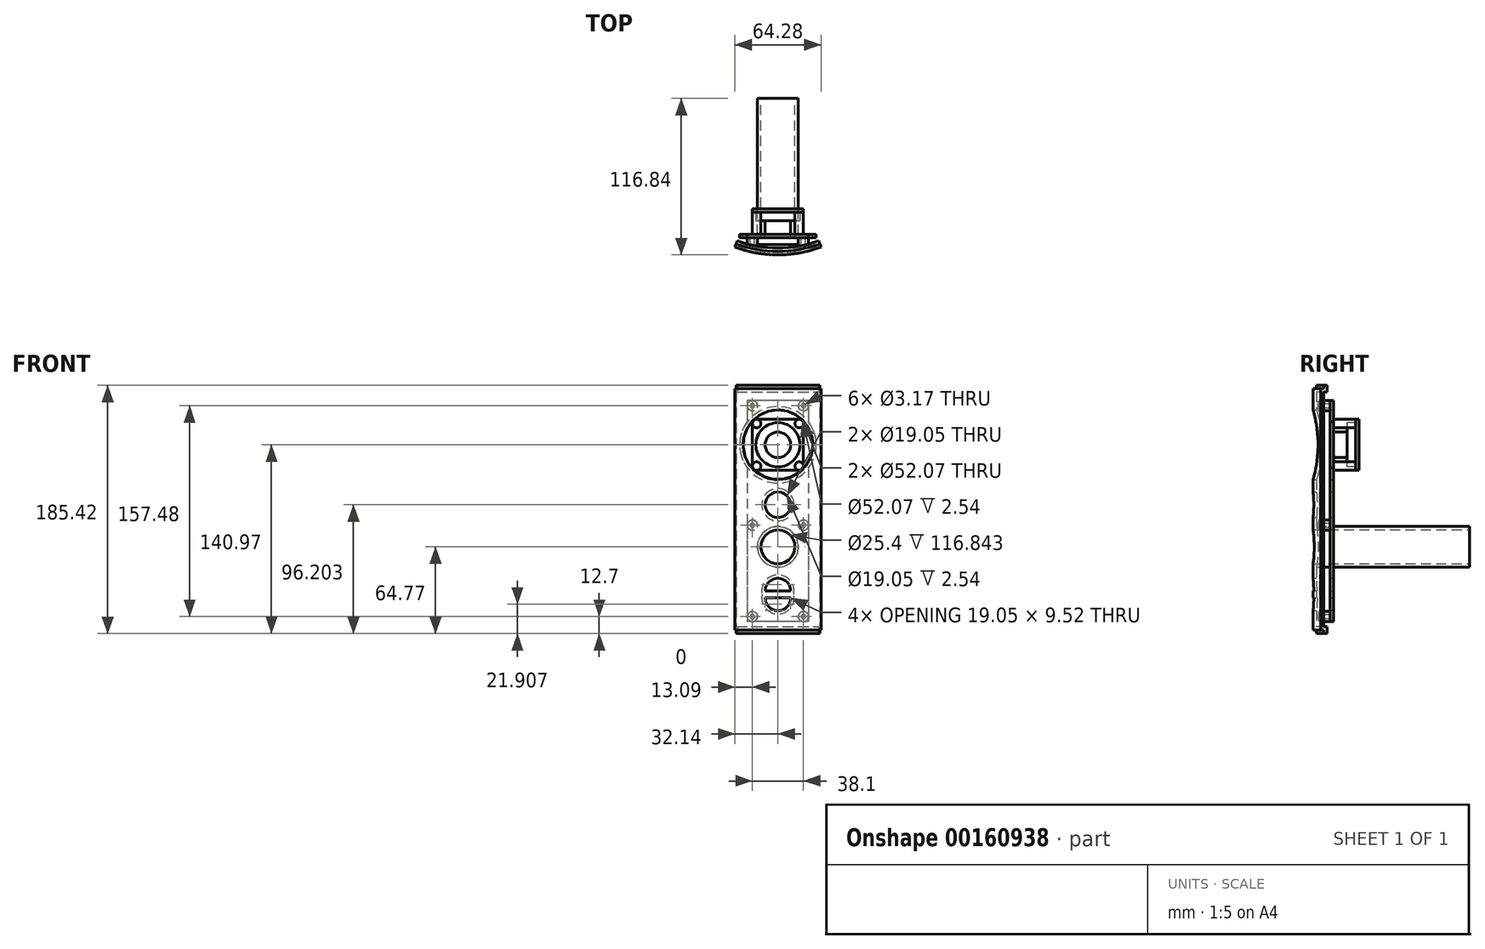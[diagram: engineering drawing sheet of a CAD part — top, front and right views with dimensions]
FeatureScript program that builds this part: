
annotation { "Feature Type Name" : "Feature", "Feature Type Description" : "" }
export const myFeature = defineFeature(function(context is Context, id is Id, definition is map)
    precondition{}
    {
        {
            var Q0;
            Q0=qCreatedBy(makeId("Front.planeOp"),FACE);
            var sketch = newSketch(context, id + "F0", { "sketchPlane" : qUnion([Q0])});
            skLineSegment(sketch, "E0.bottom", {"start": v(22.86, 179.07) * mm, "end": v(-22.86, 179.07) * mm});
            skLineSegment(sketch, "E0.top", {"start": v(22.86, 13.97) * mm, "end": v(-22.86, 13.97) * mm});
            skLineSegment(sketch, "E0.left", {"start": v(22.86, 179.07) * mm, "end": v(22.86, 163.2) * mm});
            skLineSegment(sketch, "E0.right", {"start": v(-22.86, 179.07) * mm, "end": v(-22.86, 163.2) * mm});
            skLineSegment(sketch, "E1", {"start": v(-22.86, 146.05) * mm, "end": v(22.86, 146.05) * mm, "construction": true});
            skCircle(sketch, "E2", {"center": v(0, 146.05) * mm, "radius": 9.53 * mm});
            skCircle(sketch, "E3", {"center": v(0, 146.05) * mm, "radius": 28.58 * mm});
            skCircle(sketch, "E4", {"center": v(0, 69.85) * mm, "radius": 12.7 * mm});
            skCircle(sketch, "E5", {"center": v(0, 69.85) * mm, "radius": 15.24 * mm});
            skPoint(sketch, "E6.endSnap0", {"position": v(0, 13.97) * mm});
            skLineSegment(sketch, "E7", {"start": v(0, 85.1) * mm, "end": v(0, 117.48) * mm, "construction": true});
            skPoint(sketch, "E8", {"position": v(0, 101.28) * mm});
            skCircle(sketch, "E9", {"center": v(0, 101.28) * mm, "radius": 9.53 * mm});
            skLineSegment(sketch, "E10", {"start": v(0, 54.61) * mm, "end": v(0, 13.97) * mm, "construction": true});
            skLineSegment(sketch, "E11", {"start": v(-9.52, 31.75) * mm, "end": v(9.53, 31.75) * mm});
            skPoint(sketch, "E12", {"position": v(0, 34.29) * mm});
            skPoint(sketch, "E13", {"position": v(0, 31.75) * mm});
            skArc(sketch, "E14", {"start": v(-9.52, 31.75) * mm, "mid": v(0, 22.22) * mm, "end": v(9.53, 31.75) * mm});
            skLineSegment(sketch, "E15", {"start": v(-22.86, 34.29) * mm, "end": v(22.86, 34.29) * mm, "construction": true});
            skLineSegment(sketch, "E16.MirrorCS", {"start": v(-9.52, 36.83) * mm, "end": v(9.53, 36.83) * mm});
            skArc(sketch, "E17.MirrorCS", {"start": v(-9.52, 36.83) * mm, "mid": v(0, 46.35) * mm, "end": v(9.53, 36.83) * mm});
            skCircle(sketch, "E18", {"center": v(0, 146.05) * mm, "radius": 26.04 * mm});
            skCircle(sketch, "E19", {"center": v(0, 101.28) * mm, "radius": 12.07 * mm});
            skCircle(sketch, "E20", {"center": v(0, 101.28) * mm, "radius": 6.99 * mm});
            skLineSegment(sketch, "E21.0", {"start": v(-11.8, 34.29) * mm, "end": v(11.8, 34.29) * mm});
            skArc(sketch, "E21.1", {"start": v(-11.8, 34.29) * mm, "mid": v(0, 48.9) * mm, "end": v(11.8, 34.29) * mm});
            skArc(sketch, "E22.1", {"start": v(-11.8, 34.29) * mm, "mid": v(0, 19.68) * mm, "end": v(11.8, 34.29) * mm});
            skLineSegment(sketch, "E23", {"start": v(-6.5, 29.2) * mm, "end": v(6.5, 29.2) * mm});
            skArc(sketch, "E24", {"start": v(-6.5, 29.2) * mm, "mid": v(0, 24.76) * mm, "end": v(6.5, 29.2) * mm});
            skLineSegment(sketch, "E25.MirrorCS", {"start": v(-6.5, 39.37) * mm, "end": v(6.5, 39.37) * mm});
            skArc(sketch, "E26.MirrorCS", {"start": v(-6.5, 39.37) * mm, "mid": v(0, 43.81) * mm, "end": v(6.5, 39.37) * mm});
            skLineSegment(sketch, "E27.MirrorCS", {"start": v(19.05, -58.42) * mm, "end": v(-19.05, -58.42) * mm});
            skLineSegment(sketch, "E28.MirrorCS", {"start": v(19.05, -96.52) * mm, "end": v(19.05, -58.42) * mm});
            skCircle(sketch, "E29", {"center": v(0, 146.05) * mm, "radius": 23.5 * mm});
            skLineSegment(sketch, "E30.trimOffspring", {"start": v(22.86, 128.9) * mm, "end": v(22.86, 13.97) * mm});
            skLineSegment(sketch, "E31.trimOffspring", {"start": v(-22.86, 128.9) * mm, "end": v(-22.86, 13.97) * mm});
            skCircle(sketch, "E32", {"center": v(19.05, 175.26) * mm, "radius": 3.81 * mm});
            skCircle(sketch, "E33", {"center": v(19.05, 175.26) * mm, "radius": 1.59 * mm});
            skCircle(sketch, "E34", {"center": v(-19.05, 175.26) * mm, "radius": 3.81 * mm});
            skCircle(sketch, "E35", {"center": v(-19.05, 175.26) * mm, "radius": 1.59 * mm});
            skCircle(sketch, "E36", {"center": v(-19.05, 17.78) * mm, "radius": 3.81 * mm});
            skCircle(sketch, "E37", {"center": v(-19.05, 17.78) * mm, "radius": 1.59 * mm});
            skCircle(sketch, "E38", {"center": v(19.05, 17.78) * mm, "radius": 3.81 * mm});
            skCircle(sketch, "E39", {"center": v(19.05, 17.78) * mm, "radius": 1.59 * mm});
            skCircle(sketch, "E40", {"center": v(-19.05, 86.04) * mm, "radius": 3.81 * mm});
            skCircle(sketch, "E41", {"center": v(-19.05, 86.04) * mm, "radius": 1.59 * mm});
            skCircle(sketch, "E42", {"center": v(19.05, 86.04) * mm, "radius": 3.81 * mm});
            skCircle(sketch, "E43", {"center": v(19.05, 86.04) * mm, "radius": 1.59 * mm});
            skLineSegment(sketch, "E44", {"start": v(22.86, 86.04) * mm, "end": v(-22.86, 86.04) * mm, "construction": true});
            skCircle(sketch, "E45", {"center": v(0, 146.05) * mm, "radius": 16.51 * mm});
            skSolve(sketch);
        }
        {
            var Q0;
            Q0=qCreatedBy(makeId("Front.planeOp"),FACE);
            var sketch = newSketch(context, id + "F1", { "sketchPlane" : qUnion([Q0])});
            skPoint(sketch, "E46.0", {"position": v(0, 146.05) * mm});
            skLineSegment(sketch, "E47.bottom", {"start": v(-19.05, 165.1) * mm, "end": v(19.05, 165.1) * mm});
            skLineSegment(sketch, "E47.top", {"start": v(-19.05, 127) * mm, "end": v(19.05, 127) * mm});
            skLineSegment(sketch, "E47.left", {"start": v(-19.05, 165.1) * mm, "end": v(-19.05, 127) * mm});
            skLineSegment(sketch, "E47.right", {"start": v(19.05, 165.1) * mm, "end": v(19.05, 127) * mm});
            skCircle(sketch, "E48", {"center": v(-15.88, 130.17) * mm, "radius": 3.18 * mm});
            skCircle(sketch, "E49", {"center": v(-15.88, 161.92) * mm, "radius": 3.18 * mm});
            skCircle(sketch, "E50", {"center": v(15.88, 161.92) * mm, "radius": 3.18 * mm});
            skCircle(sketch, "E51", {"center": v(15.87, 130.17) * mm, "radius": 3.18 * mm});
            skSolve(sketch);
        }
        {
            var Q0;
            {var subQ0=sQuery(id+"F0.wireOp",EDGE,"E0.left");var subQ1=sQuery(id+"F0.wireOp",EDGE,"E0.bottom");var subQ2=makeQuery(id+"F0.imprint","INTERSECT",VERTEX,{"derivedFrom":[subQ1,subQ0]});Q0=makeQuery(id+"F0.imprint","IMPRINT",FACE,{"disambiguationData":[TD([[makeQuery(id+"F0.imprint","IMPRINT",EDGE,{"disambiguationData":[TD([[subQ2,-1.0]])],"derivedFrom":subQ1}),1.0]])]});}
            var Q1;
            {var subQ0=sQuery(id+"F0.wireOp",EDGE,"E0.right");var subQ1=sQuery(id+"F0.wireOp",EDGE,"E0.bottom");var subQ2=makeQuery(id+"F0.imprint","INTERSECT",VERTEX,{"derivedFrom":[subQ1,subQ0]});Q1=makeQuery(id+"F0.imprint","IMPRINT",FACE,{"disambiguationData":[TD([[makeQuery(id+"F0.imprint","IMPRINT",EDGE,{"disambiguationData":[TD([[subQ2,1.0]])],"derivedFrom":subQ1}),1.0]])]});}
            var Q2;
            {var subQ0=sQuery(id+"F0.wireOp",EDGE,"E30.trimOffspring");var subQ1=sQuery(id+"F0.wireOp",EDGE,"E0.top");var subQ2=makeQuery(id+"F0.imprint","INTERSECT",VERTEX,{"derivedFrom":[subQ1,subQ0]});Q2=makeQuery(id+"F0.imprint","IMPRINT",FACE,{"disambiguationData":[TD([[makeQuery(id+"F0.imprint","IMPRINT",EDGE,{"disambiguationData":[TD([[subQ2,-1.0]])],"derivedFrom":subQ1}),-1.0]])]});}
            var Q3;
            {var subQ0=sQuery(id+"F0.wireOp",EDGE,"E31.trimOffspring");var subQ1=sQuery(id+"F0.wireOp",EDGE,"E0.top");var subQ2=makeQuery(id+"F0.imprint","INTERSECT",VERTEX,{"derivedFrom":[subQ1,subQ0]});Q3=makeQuery(id+"F0.imprint","IMPRINT",FACE,{"disambiguationData":[TD([[makeQuery(id+"F0.imprint","IMPRINT",EDGE,{"disambiguationData":[TD([[subQ2,1.0]])],"derivedFrom":subQ1}),-1.0]])]});}
            var Q4;
            Q4=makeQuery(id+"F0.imprint","IMPRINT",FACE,{"disambiguationData":[TD([[makeQuery(id+"F0.imprint","IMPRINT",EDGE,{"derivedFrom":sQuery(id+"F0.wireOp",EDGE,"E11")}),-1.0]])]});
            var Q5;
            Q5=makeQuery(id+"F0.imprint","IMPRINT",FACE,{"disambiguationData":[TD([[makeQuery(id+"F0.imprint","IMPRINT",EDGE,{"derivedFrom":sQuery(id+"F0.wireOp",EDGE,"E16.MirrorCS")}),1.0]])]});
            var Q6;
            Q6=makeQuery(id+"F0.imprint","IMPRINT",FACE,{"disambiguationData":[TD([[makeQuery(id+"F0.imprint","IMPRINT",EDGE,{"derivedFrom":sQuery(id+"F0.wireOp",EDGE,"E9")}),1.0]])]});
            var Q7;
            Q7=makeQuery(id+"F0.imprint","IMPRINT",FACE,{"disambiguationData":[TD([[makeQuery(id+"F0.imprint","IMPRINT",EDGE,{"derivedFrom":sQuery(id+"F0.wireOp",EDGE,"E9")}),-1.0]])]});
            var Q8;
            Q8=makeQuery(id+"F0.imprint","IMPRINT",FACE,{"disambiguationData":[TD([[makeQuery(id+"F0.imprint","IMPRINT",EDGE,{"derivedFrom":sQuery(id+"F0.wireOp",EDGE,"E16.MirrorCS")}),-1.0]])]});
            var Q9;
            Q9=makeQuery(id+"F0.imprint","IMPRINT",FACE,{"disambiguationData":[TD([[makeQuery(id+"F0.imprint","IMPRINT",EDGE,{"derivedFrom":sQuery(id+"F0.wireOp",EDGE,"E25.MirrorCS")}),1.0]])]});
            var Q10;
            Q10=makeQuery(id+"F0.imprint","IMPRINT",FACE,{"disambiguationData":[TD([[makeQuery(id+"F0.imprint","IMPRINT",EDGE,{"derivedFrom":sQuery(id+"F0.wireOp",EDGE,"E2")}),1.0]])]});
            var Q11;
            Q11=makeQuery(id+"F0.imprint","IMPRINT",FACE,{"disambiguationData":[TD([[makeQuery(id+"F0.imprint","IMPRINT",EDGE,{"derivedFrom":sQuery(id+"F0.wireOp",EDGE,"E20")}),1.0]])]});
            var Q12;
            Q12=makeQuery(id+"F0.imprint","IMPRINT",FACE,{"disambiguationData":[TD([[makeQuery(id+"F0.imprint","IMPRINT",EDGE,{"derivedFrom":sQuery(id+"F0.wireOp",EDGE,"E11")}),1.0]])]});
            var Q13;
            Q13=makeQuery(id+"F0.imprint","IMPRINT",FACE,{"disambiguationData":[TD([[makeQuery(id+"F0.imprint","IMPRINT",EDGE,{"derivedFrom":sQuery(id+"F0.wireOp",EDGE,"E23")}),-1.0]])]});
            var Q14;
            Q14=makeQuery(id+"F0.imprint","IMPRINT",FACE,{"disambiguationData":[TD([[makeQuery(id+"F0.imprint","IMPRINT",EDGE,{"derivedFrom":sQuery(id+"F0.wireOp",EDGE,"E2")}),-1.0]])]});
            var Q15;
            Q15=makeQuery(id+"F0.imprint","IMPRINT",FACE,{"disambiguationData":[TD([[makeQuery(id+"F0.imprint","IMPRINT",EDGE,{"derivedFrom":sQuery(id+"F0.wireOp",EDGE,"E18")}),1.0]])]});
            var Q16;
            Q16=makeQuery(id+"F0.imprint","IMPRINT",FACE,{"disambiguationData":[TD([[makeQuery(id+"F0.imprint","IMPRINT",EDGE,{"derivedFrom":sQuery(id+"F0.wireOp",EDGE,"E18")}),-1.0]])]});
            var Q17;
            Q17=makeQuery(id+"F0.imprint","IMPRINT",FACE,{"disambiguationData":[TD([[makeQuery(id+"F0.imprint","IMPRINT",EDGE,{"derivedFrom":sQuery(id+"F0.wireOp",EDGE,"E40")}),1.0]])]});
            var Q18;
            Q18=makeQuery(id+"F0.imprint","IMPRINT",FACE,{"disambiguationData":[TD([[makeQuery(id+"F0.imprint","IMPRINT",EDGE,{"derivedFrom":sQuery(id+"F0.wireOp",EDGE,"E35")}),-1.0]])]});
            var Q19;
            Q19=makeQuery(id+"F0.imprint","IMPRINT",FACE,{"disambiguationData":[TD([[makeQuery(id+"F0.imprint","IMPRINT",EDGE,{"derivedFrom":sQuery(id+"F0.wireOp",EDGE,"E5")}),-1.0]])]});
            var Q20;
            {var subQ7=sQuery(id+"F0.wireOp",EDGE,"E32");var subQ8=sQuery(id+"F0.wireOp",EDGE,"E0.bottom");var subQ9=makeQuery(id+"F0.imprint","INTERSECT",VERTEX,{"derivedFrom":[subQ8,subQ7]});Q20=makeQuery(id+"F0.imprint","IMPRINT",FACE,{"disambiguationData":[TD([[makeQuery(id+"F0.imprint","IMPRINT",EDGE,{"disambiguationData":[TD([[subQ9,-1.0]])],"derivedFrom":subQ8}),1.0]])]});}
            var Q21;
            Q21=makeQuery(id+"F0.imprint","IMPRINT",FACE,{"disambiguationData":[TD([[makeQuery(id+"F0.imprint","IMPRINT",EDGE,{"derivedFrom":sQuery(id+"F0.wireOp",EDGE,"E39")}),-1.0]])]});
            var Q22;
            Q22=makeQuery(id+"F0.imprint","IMPRINT",FACE,{"disambiguationData":[TD([[makeQuery(id+"F0.imprint","IMPRINT",EDGE,{"derivedFrom":sQuery(id+"F0.wireOp",EDGE,"E33")}),-1.0]])]});
            var Q23;
            Q23=makeQuery(id+"F0.imprint","IMPRINT",FACE,{"disambiguationData":[TD([[makeQuery(id+"F0.imprint","IMPRINT",EDGE,{"derivedFrom":sQuery(id+"F0.wireOp",EDGE,"E37")}),-1.0]])]});
            var Q24;
            Q24=makeQuery(id+"F0.imprint","IMPRINT",FACE,{"disambiguationData":[TD([[makeQuery(id+"F0.imprint","IMPRINT",EDGE,{"derivedFrom":sQuery(id+"F0.wireOp",EDGE,"E42")}),1.0]])]});
            var Q25;
            Q25=makeQuery(id+"F0.imprint","IMPRINT",FACE,{"disambiguationData":[TD([[makeQuery(id+"F0.imprint","IMPRINT",EDGE,{"derivedFrom":sQuery(id+"F0.wireOp",EDGE,"E29")}),1.0]])]});
            extrude(context, id + "F2", {"entities" : qUnion([Q0, Q1, Q2, Q3, Q4, Q5, Q6, Q7, Q8, Q9, Q10, Q11, Q12, Q13, Q14, Q15, Q16, Q17, Q18, Q19, Q20, Q21, Q22, Q23, Q24, Q25]), "depth" : 2.54 * mm});
        }
        {
            var Q0;
            {var subQ0=sQuery(id+"F0.wireOp",EDGE,"q9dnOXJF-SNOI-slnn-AHY7-xpP3kkiLgcJX");var subQ1=makeQuery(id+"F0.imprint","INTERSECT",VERTEX,{"derivedFrom":[sQuery(id+"F0.wireOp",EDGE,"DjAzfUVB-9j4b-ZdHd-rkEd-jADuD7Jo3FUt.bottom"),subQ0]});Q0=makeQuery(id+"F0.imprint","IMPRINT",FACE,{"disambiguationData":[TD([[makeQuery(id+"F0.imprint","IMPRINT",EDGE,{"disambiguationData":[TD([[subQ1,1.0]])],"derivedFrom":subQ0}),1.0]])]});}
            var Q1;
            {var subQ0=sQuery(id+"F0.wireOp",EDGE,"a1069b40-808e-4e41-bdb6-6fb071ad80940.MirrorC");var subQ1=makeQuery(id+"F0.imprint","INTERSECT",VERTEX,{"derivedFrom":[sQuery(id+"F0.wireOp",EDGE,"DjAzfUVB-9j4b-ZdHd-rkEd-jADuD7Jo3FUt.top"),subQ0]});Q1=makeQuery(id+"F0.imprint","IMPRINT",FACE,{"disambiguationData":[TD([[makeQuery(id+"F0.imprint","IMPRINT",EDGE,{"disambiguationData":[TD([[subQ1,1.0]])],"derivedFrom":subQ0}),-1.0]])]});}
            var Q2;
            {var subQ0=sQuery(id+"F0.wireOp",EDGE,"9b3ac167-9260-4d4f-b816-18fe052ad9fa0.MirrorC");var subQ1=makeQuery(id+"F0.imprint","INTERSECT",VERTEX,{"derivedFrom":[sQuery(id+"F0.wireOp",EDGE,"DjAzfUVB-9j4b-ZdHd-rkEd-jADuD7Jo3FUt.top"),subQ0]});Q2=makeQuery(id+"F0.imprint","IMPRINT",FACE,{"disambiguationData":[TD([[makeQuery(id+"F0.imprint","IMPRINT",EDGE,{"disambiguationData":[TD([[subQ1,1.0]])],"derivedFrom":subQ0}),1.0]])]});}
            var Q3;
            {var subQ0=sQuery(id+"F1.wireOp",EDGE,"E48");var subQ1=makeQuery(id+"F1.imprint","INTERSECT",VERTEX,{"derivedFrom":[sQuery(id+"F1.wireOp",EDGE,"E47.top"),subQ0]});Q3=makeQuery(id+"F1.imprint","IMPRINT",FACE,{"disambiguationData":[TD([[makeQuery(id+"F1.imprint","IMPRINT",EDGE,{"disambiguationData":[TD([[subQ1,1.0]])],"derivedFrom":subQ0}),1.0]])]});}
            var Q4;
            {var subQ0=sQuery(id+"F1.wireOp",EDGE,"E51");var subQ1=makeQuery(id+"F1.imprint","INTERSECT",VERTEX,{"derivedFrom":[sQuery(id+"F1.wireOp",EDGE,"E47.top"),subQ0]});Q4=makeQuery(id+"F1.imprint","IMPRINT",FACE,{"disambiguationData":[TD([[makeQuery(id+"F1.imprint","IMPRINT",EDGE,{"disambiguationData":[TD([[subQ1,1.0]])],"derivedFrom":subQ0}),1.0]])]});}
            var Q5;
            {var subQ0=sQuery(id+"F1.wireOp",EDGE,"E50");var subQ1=makeQuery(id+"F1.imprint","INTERSECT",VERTEX,{"derivedFrom":[sQuery(id+"F1.wireOp",EDGE,"E47.bottom"),subQ0]});Q5=makeQuery(id+"F1.imprint","IMPRINT",FACE,{"disambiguationData":[TD([[makeQuery(id+"F1.imprint","IMPRINT",EDGE,{"disambiguationData":[TD([[subQ1,1.0]])],"derivedFrom":subQ0}),1.0]])]});}
            var Q6;
            {var subQ0=sQuery(id+"F1.wireOp",EDGE,"E49");var subQ1=makeQuery(id+"F1.imprint","INTERSECT",VERTEX,{"derivedFrom":[sQuery(id+"F1.wireOp",EDGE,"E47.bottom"),subQ0]});Q6=makeQuery(id+"F1.imprint","IMPRINT",FACE,{"disambiguationData":[TD([[makeQuery(id+"F1.imprint","IMPRINT",EDGE,{"disambiguationData":[TD([[subQ1,-1.0]])],"derivedFrom":subQ0}),1.0]])]});}
            extrude(context, id + "F3", {"entities" : qUnion([Q0, Q1, Q2, Q3, Q4, Q5, Q6]), "operationType" : NewBodyOperationType.ADD, "oppositeDirection" : true, "depth" : 19.05 * mm});
        }
        {
            var Q0;
            Q0=makeQuery(id+"F0.imprint","IMPRINT",FACE,{"disambiguationData":[TD([[makeQuery(id+"F0.imprint","IMPRINT",EDGE,{"derivedFrom":sQuery(id+"F0.wireOp",EDGE,"E2")}),1.0]])]});
            extrude(context, id + "F4", {"entities" : qUnion([Q0]), "operationType" : NewBodyOperationType.ADD, "depth" : 16.5 * mm});
        }
        {
            var Q0;
            Q0=makeQuery(id+"F0.imprint","IMPRINT",FACE,{"disambiguationData":[TD([[makeQuery(id+"F0.imprint","IMPRINT",EDGE,{"derivedFrom":sQuery(id+"F0.wireOp",EDGE,"E2")}),1.0]])]});
            extrude(context, id + "F5", {"entities" : qUnion([Q0]), "operationType" : NewBodyOperationType.ADD, "oppositeDirection" : true, "depth" : 17.78 * mm});
        }
        {
            var Q0;
            Q0=makeQuery(id+"F0.imprint","IMPRINT",FACE,{"disambiguationData":[TD([[makeQuery(id+"F0.imprint","IMPRINT",EDGE,{"derivedFrom":sQuery(id+"F0.wireOp",EDGE,"E2")}),-1.0]])]});
            extrude(context, id + "F6", {"entities" : qUnion([Q0]), "operationType" : NewBodyOperationType.ADD, "oppositeDirection" : true, "depth" : 17.78 * mm, "hasSecondDirection" : true, "secondDirectionOppositeDirection" : true, "secondDirectionDepth" : 10.16 * mm});
        }
        {
            var Q0;
            {var subQ0=sQuery(id+"F1.wireOp",EDGE,"E50");var subQ1=makeQuery(id+"F1.imprint","INTERSECT",VERTEX,{"derivedFrom":[sQuery(id+"F1.wireOp",EDGE,"E47.bottom"),subQ0]});Q0=makeQuery(id+"F1.imprint","IMPRINT",FACE,{"disambiguationData":[TD([[makeQuery(id+"F1.imprint","IMPRINT",EDGE,{"disambiguationData":[TD([[subQ1,1.0]])],"derivedFrom":subQ0}),1.0]])]});}
            var Q1;
            {var subQ0=sQuery(id+"F1.wireOp",EDGE,"E49");var subQ1=makeQuery(id+"F1.imprint","INTERSECT",VERTEX,{"derivedFrom":[sQuery(id+"F1.wireOp",EDGE,"E47.bottom"),subQ0]});Q1=makeQuery(id+"F1.imprint","IMPRINT",FACE,{"disambiguationData":[TD([[makeQuery(id+"F1.imprint","IMPRINT",EDGE,{"disambiguationData":[TD([[subQ1,-1.0]])],"derivedFrom":subQ0}),1.0]])]});}
            var Q2;
            {var subQ0=sQuery(id+"F1.wireOp",EDGE,"E51");var subQ1=makeQuery(id+"F1.imprint","INTERSECT",VERTEX,{"derivedFrom":[sQuery(id+"F1.wireOp",EDGE,"E47.top"),subQ0]});Q2=makeQuery(id+"F1.imprint","IMPRINT",FACE,{"disambiguationData":[TD([[makeQuery(id+"F1.imprint","IMPRINT",EDGE,{"disambiguationData":[TD([[subQ1,1.0]])],"derivedFrom":subQ0}),1.0]])]});}
            var Q3;
            {var subQ5=sQuery(id+"F1.wireOp",EDGE,"E49");var subQ13=sQuery(id+"F1.wireOp",EDGE,"E47.bottom");var subQ14=makeQuery(id+"F1.imprint","INTERSECT",VERTEX,{"derivedFrom":[subQ13,subQ5]});Q3=makeQuery(id+"F1.imprint","IMPRINT",FACE,{"disambiguationData":[TD([[makeQuery(id+"F1.imprint","IMPRINT",EDGE,{"disambiguationData":[TD([[subQ14,-1.0]])],"derivedFrom":subQ13}),-1.0]])]});}
            var Q4;
            {var subQ0=sQuery(id+"F1.wireOp",EDGE,"E48");var subQ1=makeQuery(id+"F1.imprint","INTERSECT",VERTEX,{"derivedFrom":[sQuery(id+"F1.wireOp",EDGE,"E47.top"),subQ0]});Q4=makeQuery(id+"F1.imprint","IMPRINT",FACE,{"disambiguationData":[TD([[makeQuery(id+"F1.imprint","IMPRINT",EDGE,{"disambiguationData":[TD([[subQ1,1.0]])],"derivedFrom":subQ0}),1.0]])]});}
            var Q5;
            {var subQ0=sQuery(id+"F1.wireOp",EDGE,"E47.right");var subQ1=sQuery(id+"F1.wireOp",EDGE,"E47.top");var subQ2=makeQuery(id+"F1.imprint","INTERSECT",VERTEX,{"derivedFrom":[subQ1,subQ0]});Q5=makeQuery(id+"F1.imprint","IMPRINT",FACE,{"disambiguationData":[TD([[makeQuery(id+"F1.imprint","IMPRINT",EDGE,{"disambiguationData":[TD([[subQ2,1.0]])],"derivedFrom":subQ1}),1.0]])]});}
            var Q6;
            {var subQ0=sQuery(id+"F1.wireOp",EDGE,"E47.left");var subQ1=sQuery(id+"F1.wireOp",EDGE,"E47.top");var subQ2=makeQuery(id+"F1.imprint","INTERSECT",VERTEX,{"derivedFrom":[subQ1,subQ0]});Q6=makeQuery(id+"F1.imprint","IMPRINT",FACE,{"disambiguationData":[TD([[makeQuery(id+"F1.imprint","IMPRINT",EDGE,{"disambiguationData":[TD([[subQ2,-1.0]])],"derivedFrom":subQ1}),1.0]])]});}
            var Q7;
            {var subQ0=sQuery(id+"F1.wireOp",EDGE,"E47.left");var subQ1=sQuery(id+"F1.wireOp",EDGE,"E47.bottom");var subQ2=makeQuery(id+"F1.imprint","INTERSECT",VERTEX,{"derivedFrom":[subQ1,subQ0]});Q7=makeQuery(id+"F1.imprint","IMPRINT",FACE,{"disambiguationData":[TD([[makeQuery(id+"F1.imprint","IMPRINT",EDGE,{"disambiguationData":[TD([[subQ2,-1.0]])],"derivedFrom":subQ1}),-1.0]])]});}
            var Q8;
            {var subQ0=sQuery(id+"F1.wireOp",EDGE,"E47.right");var subQ1=sQuery(id+"F1.wireOp",EDGE,"E47.bottom");var subQ2=makeQuery(id+"F1.imprint","INTERSECT",VERTEX,{"derivedFrom":[subQ1,subQ0]});Q8=makeQuery(id+"F1.imprint","IMPRINT",FACE,{"disambiguationData":[TD([[makeQuery(id+"F1.imprint","IMPRINT",EDGE,{"disambiguationData":[TD([[subQ2,1.0]])],"derivedFrom":subQ1}),-1.0]])]});}
            extrude(context, id + "F7", {"entities" : qUnion([Q0, Q1, Q2, Q3, Q4, Q5, Q6, Q7, Q8]), "operationType" : NewBodyOperationType.ADD, "oppositeDirection" : true, "depth" : 19.05 * mm, "hasSecondDirection" : true, "secondDirectionOppositeDirection" : true, "secondDirectionDepth" : 16.5 * mm});
        }
        {
            var Q0;
            Q0=makeQuery(id+"F0.imprint","IMPRINT",FACE,{"disambiguationData":[TD([[makeQuery(id+"F0.imprint","IMPRINT",EDGE,{"derivedFrom":sQuery(id+"F0.wireOp",EDGE,"E23")}),-1.0]])]});
            var Q1;
            Q1=makeQuery(id+"F0.imprint","IMPRINT",FACE,{"disambiguationData":[TD([[makeQuery(id+"F0.imprint","IMPRINT",EDGE,{"derivedFrom":sQuery(id+"F0.wireOp",EDGE,"E25.MirrorCS")}),1.0]])]});
            var Q2;
            Q2=makeQuery(id+"F0.imprint","IMPRINT",FACE,{"disambiguationData":[TD([[makeQuery(id+"F0.imprint","IMPRINT",EDGE,{"derivedFrom":sQuery(id+"F0.wireOp",EDGE,"E20")}),1.0]])]});
            var Q3;
            Q3=makeQuery(id+"F0.imprint","IMPRINT",FACE,{"disambiguationData":[TD([[makeQuery(id+"F0.imprint","IMPRINT",EDGE,{"derivedFrom":sQuery(id+"F0.wireOp",EDGE,"E2")}),-1.0]])]});
            var Q4;
            Q4=makeQuery(id+"F0.imprint","IMPRINT",FACE,{"disambiguationData":[TD([[makeQuery(id+"F0.imprint","IMPRINT",EDGE,{"derivedFrom":sQuery(id+"F0.wireOp",EDGE,"E2")}),1.0]])]});
            extrude(context, id + "F8", {"entities" : qUnion([Q0, Q1, Q2, Q3, Q4]), "operationType" : NewBodyOperationType.ADD, "depth" : 10.16 * mm});
        }
        {
            var Q0;
            Q0=makeQuery(id+"F0.imprint","IMPRINT",FACE,{"disambiguationData":[TD([[makeQuery(id+"F0.imprint","IMPRINT",EDGE,{"derivedFrom":sQuery(id+"F0.wireOp",EDGE,"E18")}),-1.0]])]});
            var Q1;
            Q1=makeQuery(id+"F0.imprint","IMPRINT",FACE,{"disambiguationData":[TD([[makeQuery(id+"F0.imprint","IMPRINT",EDGE,{"derivedFrom":sQuery(id+"F0.wireOp",EDGE,"E9")}),-1.0]])]});
            var Q2;
            Q2=makeQuery(id+"F0.imprint","IMPRINT",FACE,{"disambiguationData":[TD([[makeQuery(id+"F0.imprint","IMPRINT",EDGE,{"derivedFrom":sQuery(id+"F0.wireOp",EDGE,"E16.MirrorCS")}),-1.0]])]});
            var Q3;
            Q3=makeQuery(id+"F0.imprint","IMPRINT",FACE,{"disambiguationData":[TD([[makeQuery(id+"F0.imprint","IMPRINT",EDGE,{"derivedFrom":sQuery(id+"F0.wireOp",EDGE,"E11")}),1.0]])]});
            extrude(context, id + "F9", {"entities" : qUnion([Q0, Q1, Q2, Q3]), "depth" : 10.16 * mm, "hasSecondDirection" : true, "secondDirectionOppositeDirection" : false, "secondDirectionDepth" : 7.62 * mm});
        }
        {
            var Q0;
            Q0=makeQuery(id+"F0.imprint","IMPRINT",FACE,{"disambiguationData":[TD([[makeQuery(id+"F0.imprint","IMPRINT",EDGE,{"derivedFrom":sQuery(id+"F0.wireOp",EDGE,"E18")}),1.0]])]});
            var Q1;
            Q1=makeQuery(id+"F0.imprint","IMPRINT",FACE,{"disambiguationData":[TD([[makeQuery(id+"F0.imprint","IMPRINT",EDGE,{"derivedFrom":sQuery(id+"F0.wireOp",EDGE,"E9")}),1.0]])]});
            var Q2;
            Q2=makeQuery(id+"F0.imprint","IMPRINT",FACE,{"disambiguationData":[TD([[makeQuery(id+"F0.imprint","IMPRINT",EDGE,{"derivedFrom":sQuery(id+"F0.wireOp",EDGE,"E11")}),-1.0]])]});
            var Q3;
            Q3=makeQuery(id+"F0.imprint","IMPRINT",FACE,{"disambiguationData":[TD([[makeQuery(id+"F0.imprint","IMPRINT",EDGE,{"derivedFrom":sQuery(id+"F0.wireOp",EDGE,"E16.MirrorCS")}),1.0]])]});
            extrude(context, id + "F10", {"entities" : qUnion([Q0, Q1, Q2, Q3]), "operationType" : NewBodyOperationType.ADD, "depth" : 15.24 * mm, "hasSecondDirection" : true, "secondDirectionOppositeDirection" : false, "secondDirectionDepth" : 7.62 * mm});
        }
        {
            var Q0;
            Q0=makeQuery(id+"F0.imprint","IMPRINT",FACE,{"disambiguationData":[TD([[makeQuery(id+"F0.imprint","IMPRINT",EDGE,{"derivedFrom":sQuery(id+"F0.wireOp",EDGE,"E2")}),-1.0]])]});
            var Q1;
            Q1=makeQuery(id+"F0.imprint","IMPRINT",FACE,{"disambiguationData":[TD([[makeQuery(id+"F0.imprint","IMPRINT",EDGE,{"derivedFrom":sQuery(id+"F0.wireOp",EDGE,"E20")}),1.0]])]});
            var Q2;
            Q2=makeQuery(id+"F0.imprint","IMPRINT",FACE,{"disambiguationData":[TD([[makeQuery(id+"F0.imprint","IMPRINT",EDGE,{"derivedFrom":sQuery(id+"F0.wireOp",EDGE,"E25.MirrorCS")}),1.0]])]});
            var Q3;
            Q3=makeQuery(id+"F0.imprint","IMPRINT",FACE,{"disambiguationData":[TD([[makeQuery(id+"F0.imprint","IMPRINT",EDGE,{"derivedFrom":sQuery(id+"F0.wireOp",EDGE,"E23")}),-1.0]])]});
            var Q4;
            Q4=makeQuery(id+"F0.imprint","IMPRINT",FACE,{"disambiguationData":[TD([[makeQuery(id+"F0.imprint","IMPRINT",EDGE,{"derivedFrom":sQuery(id+"F0.wireOp",EDGE,"E29")}),1.0]])]});
            extrude(context, id + "F11", {"entities" : qUnion([Q0, Q1, Q2, Q3, Q4]), "operationType" : NewBodyOperationType.ADD, "depth" : 15.24 * mm, "hasSecondDirection" : true, "secondDirectionOppositeDirection" : false, "secondDirectionDepth" : 12.7 * mm});
        }
        {
            var Q0;
            Q0=qCreatedBy(makeId("Top.planeOp"),FACE);
            var sketch = newSketch(context, id + "F12", { "sketchPlane" : qUnion([Q0])});
            skLineSegment(sketch, "E52", {"start": v(0, -68.95) * mm, "end": v(0, 232.52) * mm, "construction": true});
            skCircle(sketch, "E53", {"center": v(0, 78.74) * mm, "radius": 93.98 * mm});
            skCircle(sketch, "E54", {"center": v(0, 78.74) * mm, "radius": 91.44 * mm});
            skCircle(sketch, "E55", {"center": v(0, 78.74) * mm, "radius": 88.9 * mm});
            skLineSegment(sketch, "E56", {"start": v(0, 78.74) * mm, "end": v(-32.14, -9.57) * mm});
            skLineSegment(sketch, "E57.MirrorCS", {"start": v(0, 78.74) * mm, "end": v(32.14, -9.57) * mm});
            skSolve(sketch);
        }
        {
            var Q0;
            {var subQ0=sQuery(id+"F12.wireOp",EDGE,"E56");var subQ1=sQuery(id+"F12.wireOp",EDGE,"E53");var subQ2=makeQuery(id+"F12.imprint","INTERSECT",VERTEX,{"derivedFrom":[subQ1,subQ0]});Q0=makeQuery(id+"F12.imprint","IMPRINT",FACE,{"disambiguationData":[TD([[makeQuery(id+"F12.imprint","IMPRINT",EDGE,{"disambiguationData":[TD([[subQ2,-1.0]])],"derivedFrom":subQ1}),1.0]])]});}
            extrude(context, id + "F13", {"entities" : qUnion([Q0]), "depth" : 187.96 * mm, "hasSecondDirection" : true, "secondDirectionOppositeDirection" : false, "secondDirectionDepth" : 7.62 * mm});
        }
        {
            var Q0;
            Q0=makeQuery(id+"F0.imprint","IMPRINT",FACE,{"disambiguationData":[TD([[makeQuery(id+"F0.imprint","IMPRINT",EDGE,{"derivedFrom":sQuery(id+"F0.wireOp",EDGE,"E2")}),-1.0]])]});
            var Q1;
            Q1=makeQuery(id+"F0.imprint","IMPRINT",FACE,{"disambiguationData":[TD([[makeQuery(id+"F0.imprint","IMPRINT",EDGE,{"derivedFrom":sQuery(id+"F0.wireOp",EDGE,"E18")}),1.0]])]});
            var Q2;
            Q2=makeQuery(id+"F0.imprint","IMPRINT",FACE,{"disambiguationData":[TD([[makeQuery(id+"F0.imprint","IMPRINT",EDGE,{"derivedFrom":sQuery(id+"F0.wireOp",EDGE,"E2")}),1.0]])]});
            var Q3;
            Q3=makeQuery(id+"F0.imprint","IMPRINT",FACE,{"disambiguationData":[TD([[makeQuery(id+"F0.imprint","IMPRINT",EDGE,{"derivedFrom":sQuery(id+"F0.wireOp",EDGE,"E9")}),1.0]])]});
            var Q4;
            Q4=makeQuery(id+"F0.imprint","IMPRINT",FACE,{"disambiguationData":[TD([[makeQuery(id+"F0.imprint","IMPRINT",EDGE,{"derivedFrom":sQuery(id+"F0.wireOp",EDGE,"E20")}),1.0]])]});
            var Q5;
            Q5=makeQuery(id+"F0.imprint","IMPRINT",FACE,{"disambiguationData":[TD([[makeQuery(id+"F0.imprint","IMPRINT",EDGE,{"derivedFrom":sQuery(id+"F0.wireOp",EDGE,"E4")}),1.0]])]});
            var Q6;
            Q6=makeQuery(id+"F0.imprint","IMPRINT",FACE,{"disambiguationData":[TD([[makeQuery(id+"F0.imprint","IMPRINT",EDGE,{"derivedFrom":sQuery(id+"F0.wireOp",EDGE,"E25.MirrorCS")}),1.0]])]});
            var Q7;
            Q7=makeQuery(id+"F0.imprint","IMPRINT",FACE,{"disambiguationData":[TD([[makeQuery(id+"F0.imprint","IMPRINT",EDGE,{"derivedFrom":sQuery(id+"F0.wireOp",EDGE,"E16.MirrorCS")}),1.0]])]});
            var Q8;
            Q8=makeQuery(id+"F0.imprint","IMPRINT",FACE,{"disambiguationData":[TD([[makeQuery(id+"F0.imprint","IMPRINT",EDGE,{"derivedFrom":sQuery(id+"F0.wireOp",EDGE,"E11")}),-1.0]])]});
            var Q9;
            Q9=makeQuery(id+"F0.imprint","IMPRINT",FACE,{"disambiguationData":[TD([[makeQuery(id+"F0.imprint","IMPRINT",EDGE,{"derivedFrom":sQuery(id+"F0.wireOp",EDGE,"E23")}),-1.0]])]});
            var Q10;
            Q10=makeQuery(id+"F0.imprint","IMPRINT",FACE,{"disambiguationData":[TD([[makeQuery(id+"F0.imprint","IMPRINT",EDGE,{"derivedFrom":sQuery(id+"F0.wireOp",EDGE,"E29")}),1.0]])]});
            extrude(context, id + "F14", {"entities" : qUnion([Q0, Q1, Q2, Q3, Q4, Q5, Q6, Q7, Q8, Q9, Q10]), "operationType" : NewBodyOperationType.REMOVE, "depth" : 25.4 * mm});
        }
        {
            var Q0;
            Q0=makeQuery(id+"F0.imprint","IMPRINT",FACE,{"disambiguationData":[TD([[makeQuery(id+"F0.imprint","IMPRINT",EDGE,{"derivedFrom":sQuery(id+"F0.wireOp",EDGE,"E4")}),-1.0]])]});
            extrude(context, id + "F15", {"entities" : qUnion([Q0]), "operationType" : NewBodyOperationType.ADD, "endBound" : BoundingType.UP_TO_NEXT, "depth" : 25.4 * mm, "hasSecondDirection" : true, "secondDirectionOppositeDirection" : true, "secondDirectionDepth" : 101.6 * mm});
        }
        {
            var Q0;
            {var subQ0=sQuery(id+"F12.wireOp",EDGE,"E56");var subQ1=sQuery(id+"F12.wireOp",EDGE,"E54");var subQ2=makeQuery(id+"F12.imprint","INTERSECT",VERTEX,{"derivedFrom":[subQ1,subQ0]});Q0=makeQuery(id+"F12.imprint","IMPRINT",FACE,{"disambiguationData":[TD([[makeQuery(id+"F12.imprint","IMPRINT",EDGE,{"disambiguationData":[TD([[subQ2,-1.0]])],"derivedFrom":subQ1}),1.0]])]});}
            extrude(context, id + "F16", {"entities" : qUnion([Q0]), "operationType" : NewBodyOperationType.ADD, "depth" : 10.16 * mm, "hasSecondDirection" : true, "secondDirectionOppositeDirection" : false, "secondDirectionDepth" : 5.08 * mm});
        }
        {
            var Q0;
            {var subQ0=sQuery(id+"F12.wireOp",EDGE,"E56");var subQ1=sQuery(id+"F12.wireOp",EDGE,"E54");var subQ2=makeQuery(id+"F12.imprint","INTERSECT",VERTEX,{"derivedFrom":[subQ1,subQ0]});Q0=makeQuery(id+"F12.imprint","IMPRINT",FACE,{"disambiguationData":[TD([[makeQuery(id+"F12.imprint","IMPRINT",EDGE,{"disambiguationData":[TD([[subQ2,-1.0]])],"derivedFrom":subQ1}),1.0]])]});}
            extrude(context, id + "F17", {"entities" : qUnion([Q0]), "operationType" : NewBodyOperationType.ADD, "depth" : 190.5 * mm, "hasSecondDirection" : true, "secondDirectionOppositeDirection" : false, "secondDirectionDepth" : 185.42 * mm});
        }
        {
            var Q0;
            Q0=makeQuery(id+"F0.imprint","IMPRINT",FACE,{"disambiguationData":[TD([[makeQuery(id+"F0.imprint","IMPRINT",EDGE,{"derivedFrom":sQuery(id+"F0.wireOp",EDGE,"E33")}),-1.0]])]});
            var Q1;
            Q1=makeQuery(id+"F0.imprint","IMPRINT",FACE,{"disambiguationData":[TD([[makeQuery(id+"F0.imprint","IMPRINT",EDGE,{"derivedFrom":sQuery(id+"F0.wireOp",EDGE,"E35")}),-1.0]])]});
            var Q2;
            Q2=makeQuery(id+"F0.imprint","IMPRINT",FACE,{"disambiguationData":[TD([[makeQuery(id+"F0.imprint","IMPRINT",EDGE,{"derivedFrom":sQuery(id+"F0.wireOp",EDGE,"E40")}),1.0]])]});
            var Q3;
            Q3=makeQuery(id+"F0.imprint","IMPRINT",FACE,{"disambiguationData":[TD([[makeQuery(id+"F0.imprint","IMPRINT",EDGE,{"derivedFrom":sQuery(id+"F0.wireOp",EDGE,"E42")}),1.0]])]});
            var Q4;
            Q4=makeQuery(id+"F0.imprint","IMPRINT",FACE,{"disambiguationData":[TD([[makeQuery(id+"F0.imprint","IMPRINT",EDGE,{"derivedFrom":sQuery(id+"F0.wireOp",EDGE,"E39")}),-1.0]])]});
            var Q5;
            Q5=makeQuery(id+"F0.imprint","IMPRINT",FACE,{"disambiguationData":[TD([[makeQuery(id+"F0.imprint","IMPRINT",EDGE,{"derivedFrom":sQuery(id+"F0.wireOp",EDGE,"E37")}),-1.0]])]});
            var Q6;
            Q6=makeQuery(id+"F13.opExtrude","SWEPT_BODY",BODY,{"disambiguationData":[OSD([sQuery(id+"F12.wireOp",EDGE,"E53"),sQuery(id+"F12.wireOp",EDGE,"E54"),sQuery(id+"F12.wireOp",EDGE,"E56"),sQuery(id+"F12.wireOp",EDGE,"E57.MirrorCS")])]});
            extrude(context, id + "F18", {"entities" : qUnion([Q0, Q1, Q2, Q3, Q4, Q5]), "operationType" : NewBodyOperationType.ADD, "endBound" : BoundingType.UP_TO_BODY, "endBoundEntityBody" : qUnion([Q6]), "depth" : 25.4 * mm, "hasSecondDirection" : true, "secondDirectionOppositeDirection" : false, "secondDirectionDepth" : 2.54 * mm});
        }
    });
